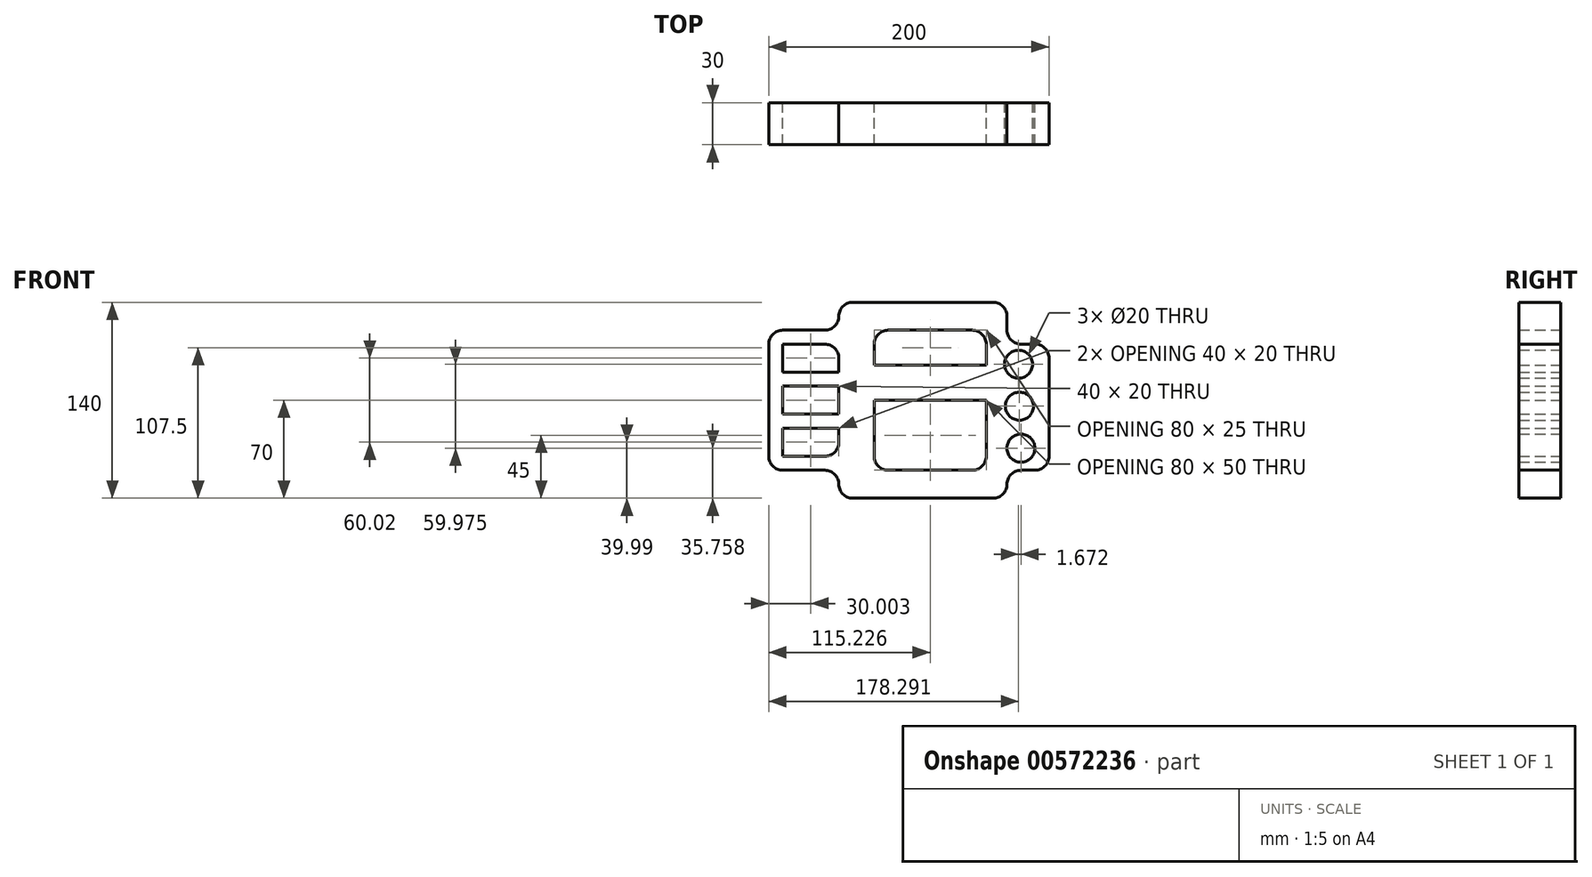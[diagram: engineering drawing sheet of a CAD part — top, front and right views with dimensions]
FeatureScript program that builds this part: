
annotation { "Feature Type Name" : "Feature", "Feature Type Description" : "" }
export const myFeature = defineFeature(function(context is Context, id is Id, definition is map)
    precondition{}
    {
        {
            var Q0;
            Q0=qCreatedBy(makeId("Front.planeOp"),FACE);
            var sketch = newSketch(context, id + "F0", { "sketchPlane" : qUnion([Q0])});
            skLineSegment(sketch, "E0", {"start": v(-24.27, 90) * mm, "end": v(75.73, 90) * mm});
            skLineSegment(sketch, "E1", {"start": v(85.73, 80) * mm, "end": v(85.73, 70.1) * mm});
            skLineSegment(sketch, "E2", {"start": v(95.73, 60.1) * mm, "end": v(105.73, 60.1) * mm});
            skLineSegment(sketch, "E3", {"start": v(115.73, 50.1) * mm, "end": v(115.73, -20) * mm});
            skLineSegment(sketch, "E4", {"start": v(105.73, -30) * mm, "end": v(95.73, -30) * mm});
            skLineSegment(sketch, "E5", {"start": v(85.73, -40) * mm, "end": v(85.73, -40) * mm});
            skLineSegment(sketch, "E6", {"start": v(75.73, -50) * mm, "end": v(-24.27, -50) * mm});
            skLineSegment(sketch, "E7", {"start": v(-34.27, -40) * mm, "end": v(-34.27, -40) * mm});
            skLineSegment(sketch, "E8", {"start": v(-44.27, -30) * mm, "end": v(-74.27, -30) * mm});
            skLineSegment(sketch, "E9", {"start": v(-84.27, -20) * mm, "end": v(-84.27, 60) * mm});
            skLineSegment(sketch, "E10", {"start": v(-74.27, 70) * mm, "end": v(-44.27, 70) * mm});
            skLineSegment(sketch, "E11", {"start": v(-34.27, 80) * mm, "end": v(-34.27, 80) * mm});
            skLineSegment(sketch, "E12", {"start": v(0.96, 70) * mm, "end": v(60.96, 70) * mm});
            skLineSegment(sketch, "E13", {"start": v(70.96, 60) * mm, "end": v(70.96, 45) * mm});
            skLineSegment(sketch, "E14", {"start": v(60.96, -30) * mm, "end": v(0.96, -30) * mm});
            skLineSegment(sketch, "E15", {"start": v(-9.04, -20) * mm, "end": v(-9.04, 20) * mm});
            skLineSegment(sketch, "E16", {"start": v(-9.04, 45) * mm, "end": v(70.96, 45) * mm});
            skLineSegment(sketch, "E17", {"start": v(70.96, 20) * mm, "end": v(-9.04, 20) * mm});
            skLineSegment(sketch, "E18.trimOffspring", {"start": v(-9.04, 45) * mm, "end": v(-9.04, 60) * mm});
            skLineSegment(sketch, "E19.trimOffspring", {"start": v(70.96, 20) * mm, "end": v(70.96, -20) * mm});
            skCircle(sketch, "E20", {"center": v(94.02, 45.74) * mm, "radius": 10 * mm});
            skCircle(sketch, "E21", {"center": v(95.7, -14.23) * mm, "radius": 10 * mm});
            skCircle(sketch, "E22", {"center": v(94.66, 15.75) * mm, "radius": 10 * mm});
            skLineSegment(sketch, "E23", {"start": v(-74.27, 60.02) * mm, "end": v(-74.27, 40.02) * mm});
            skLineSegment(sketch, "E24", {"start": v(-74.27, -20) * mm, "end": v(-44.27, -20) * mm});
            skLineSegment(sketch, "E25", {"start": v(-34.27, -10) * mm, "end": v(-34.27, 0) * mm});
            skLineSegment(sketch, "E26", {"start": v(-44.27, 60.02) * mm, "end": v(-74.27, 60.02) * mm});
            skLineSegment(sketch, "E27", {"start": v(-74.27, 40.02) * mm, "end": v(-34.27, 40.02) * mm});
            skLineSegment(sketch, "E28", {"start": v(-34.27, 30) * mm, "end": v(-74.27, 30) * mm});
            skLineSegment(sketch, "E29", {"start": v(-74.27, 10) * mm, "end": v(-34.27, 10) * mm});
            skLineSegment(sketch, "E30", {"start": v(-34.27, 0) * mm, "end": v(-74.27, 0) * mm});
            skLineSegment(sketch, "E31.trimOffspring", {"start": v(-34.27, 10) * mm, "end": v(-34.27, 30) * mm});
            skLineSegment(sketch, "E32.trimOffspring", {"start": v(-74.27, 0) * mm, "end": v(-74.27, -20) * mm});
            skLineSegment(sketch, "E33.trimOffspring", {"start": v(-74.27, 30) * mm, "end": v(-74.27, 10) * mm});
            skLineSegment(sketch, "E34.trimOffspring", {"start": v(-34.27, 40.02) * mm, "end": v(-34.27, 50.02) * mm});
            skPoint(sketch, "E35.visualSharp", {"position": v(85.73, 60.1) * mm});
            skArc(sketch, "E35.filletArc", {"start": v(85.73, 70.1) * mm, "mid": v(88.66, 63.03) * mm, "end": v(95.73, 60.1) * mm});
            skPoint(sketch, "E36.visualSharp", {"position": v(-34.27, 70) * mm});
            skArc(sketch, "E36.filletArc", {"start": v(-44.27, 70) * mm, "mid": v(-37.2, 72.94) * mm, "end": v(-34.27, 80) * mm});
            skPoint(sketch, "E37.visualSharp", {"position": v(85.73, -30) * mm});
            skArc(sketch, "E37.filletArc", {"start": v(95.73, -30) * mm, "mid": v(88.66, -32.92) * mm, "end": v(85.73, -40) * mm});
            skPoint(sketch, "E38.visualSharp", {"position": v(-34.27, -30) * mm});
            skArc(sketch, "E38.filletArc", {"start": v(-34.27, -40) * mm, "mid": v(-37.2, -32.92) * mm, "end": v(-44.27, -30) * mm});
            skPoint(sketch, "E39.visualSharp", {"position": v(-84.27, 70) * mm});
            skArc(sketch, "E39.filletArc", {"start": v(-74.27, 70) * mm, "mid": v(-81.34, 67.08) * mm, "end": v(-84.27, 60) * mm});
            skPoint(sketch, "E40.visualSharp", {"position": v(85.73, 90) * mm});
            skArc(sketch, "E40.filletArc", {"start": v(85.73, 80) * mm, "mid": v(82.8, 87.08) * mm, "end": v(75.73, 90) * mm});
            skPoint(sketch, "E41.visualSharp", {"position": v(-34.27, 90) * mm});
            skArc(sketch, "E41.filletArc", {"start": v(-24.27, 90) * mm, "mid": v(-31.34, 87.08) * mm, "end": v(-34.27, 80) * mm});
            skPoint(sketch, "E42.visualSharp", {"position": v(115.73, 60.1) * mm});
            skArc(sketch, "E42.filletArc", {"start": v(115.73, 50.1) * mm, "mid": v(112.8, 57.17) * mm, "end": v(105.73, 60.1) * mm});
            skPoint(sketch, "E43.visualSharp", {"position": v(115.73, -30) * mm});
            skArc(sketch, "E43.filletArc", {"start": v(105.73, -30) * mm, "mid": v(112.8, -27.06) * mm, "end": v(115.73, -20) * mm});
            skPoint(sketch, "E44.visualSharp", {"position": v(85.73, -50) * mm});
            skArc(sketch, "E44.filletArc", {"start": v(75.73, -50) * mm, "mid": v(82.8, -47.06) * mm, "end": v(85.73, -40) * mm});
            skPoint(sketch, "E45.visualSharp", {"position": v(-34.27, -50) * mm});
            skArc(sketch, "E45.filletArc", {"start": v(-34.27, -40) * mm, "mid": v(-31.34, -47.06) * mm, "end": v(-24.27, -50) * mm});
            skPoint(sketch, "E46.visualSharp", {"position": v(-84.27, -30) * mm});
            skArc(sketch, "E46.filletArc", {"start": v(-84.27, -20) * mm, "mid": v(-81.34, -27.06) * mm, "end": v(-74.27, -30) * mm});
            skPoint(sketch, "E47.visualSharp", {"position": v(-34.27, 60.02) * mm});
            skArc(sketch, "E47.filletArc", {"start": v(-34.27, 50.02) * mm, "mid": v(-37.2, 57.1) * mm, "end": v(-44.27, 60.02) * mm});
            skPoint(sketch, "E48.visualSharp", {"position": v(-34.27, -20) * mm});
            skArc(sketch, "E48.filletArc", {"start": v(-44.27, -20) * mm, "mid": v(-37.2, -17.07) * mm, "end": v(-34.27, -10) * mm});
            skPoint(sketch, "E49.visualSharp", {"position": v(70.96, 70) * mm});
            skArc(sketch, "E49.filletArc", {"start": v(70.96, 60) * mm, "mid": v(68.03, 67.08) * mm, "end": v(60.96, 70) * mm});
            skPoint(sketch, "E50.visualSharp", {"position": v(-9.04, 70) * mm});
            skArc(sketch, "E50.filletArc", {"start": v(0.96, 70) * mm, "mid": v(-6.12, 67.08) * mm, "end": v(-9.04, 60) * mm});
            skPoint(sketch, "E51.visualSharp", {"position": v(-9.04, -30) * mm});
            skArc(sketch, "E51.filletArc", {"start": v(-9.04, -20) * mm, "mid": v(-6.12, -27.06) * mm, "end": v(0.96, -30) * mm});
            skPoint(sketch, "E52.visualSharp", {"position": v(70.96, -30) * mm});
            skArc(sketch, "E52.filletArc", {"start": v(60.96, -30) * mm, "mid": v(68.03, -27.06) * mm, "end": v(70.96, -20) * mm});
            skSolve(sketch);
        }
        {
            var Q0;
            Q0 = qSketchRegion(id + "F0", true);
            extrude(context, id + "F1", {"entities" : qUnion([Q0]), "depth" : 30 * mm, "offsetDistance" : 25 * mm});
        }
    });
